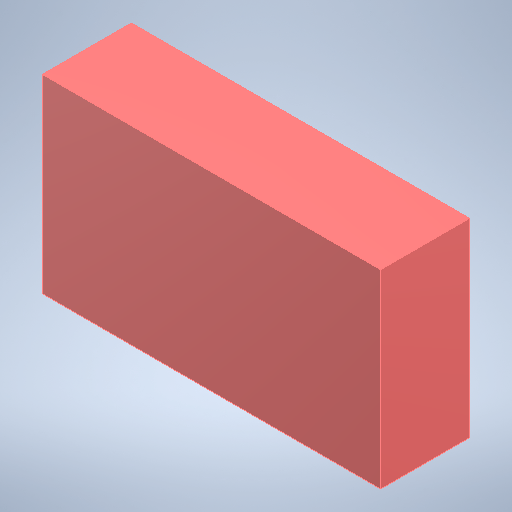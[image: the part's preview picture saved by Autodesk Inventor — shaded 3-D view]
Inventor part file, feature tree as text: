
AUTODESK INVENTOR PART (.ipt)
format: ipt  version: 2025.1 (Build 291241000, 241)  size: 186,368 bytes
history: native  units: mm
features: other x1, extrude x1, sketch x1
ambient origin geometry x8: Origin, YZ Plane, XZ Plane, XY Plane, X Axis, Y Axis, Z Axis, Center Point
bodies: Body1 (feature_tree)
feature tree (3):
  other  "ソリッド1"
  extrude  "押し出し1"  Depth=57.0mm
  sketch  "スケッチ1"
